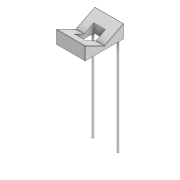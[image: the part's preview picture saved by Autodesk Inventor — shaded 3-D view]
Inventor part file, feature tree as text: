
AUTODESK INVENTOR PART (.ipt)
format: ipt  version: 2020 (Build 240168000, 168)  size: 139,776 bytes
history: native  units: mm
features: extrude x4, sketch x4, chamfer x1
ambient origin geometry x8: Origin, YZ Plane, XZ Plane, XY Plane, X Axis, Y Axis, Z Axis, Center Point
bodies: Volumenkörper1 (feature_tree)
feature tree (9):
  extrude  "Extrusion1"  Depth=200.0mm
  extrude  "Extrusion2"  Depth=10.0mm
  extrude  "Extrusion3"  Depth=200.0mm
  chamfer  "Fase2"  Distance=10.0mm
  extrude  "Extrusion4"  Depth=100.0mm
  sketch  "Skizze1"  dims[d0=150.0mm d1=200.0mm]
  sketch  "Skizze2"  dims[d2=20.0mm d3=0.0mm d4=10.0mm]
  sketch  "Skizze5"  dims[d5=10.0mm d6=200.0mm]
  sketch  "Skizze6"  dims[d7=20.0mm d8=10.0mm d9=20.0mm d10=10.0mm d11=500.0mm d12=0.0mm d17=70.0mm d18=70.0mm d19=113.5mm d20=0.0mm d21=2.0mm d22=2.0mm d23=45.0deg d24=60.0mm d25=100.0mm d26=0.0mm d27=0.0mm]
